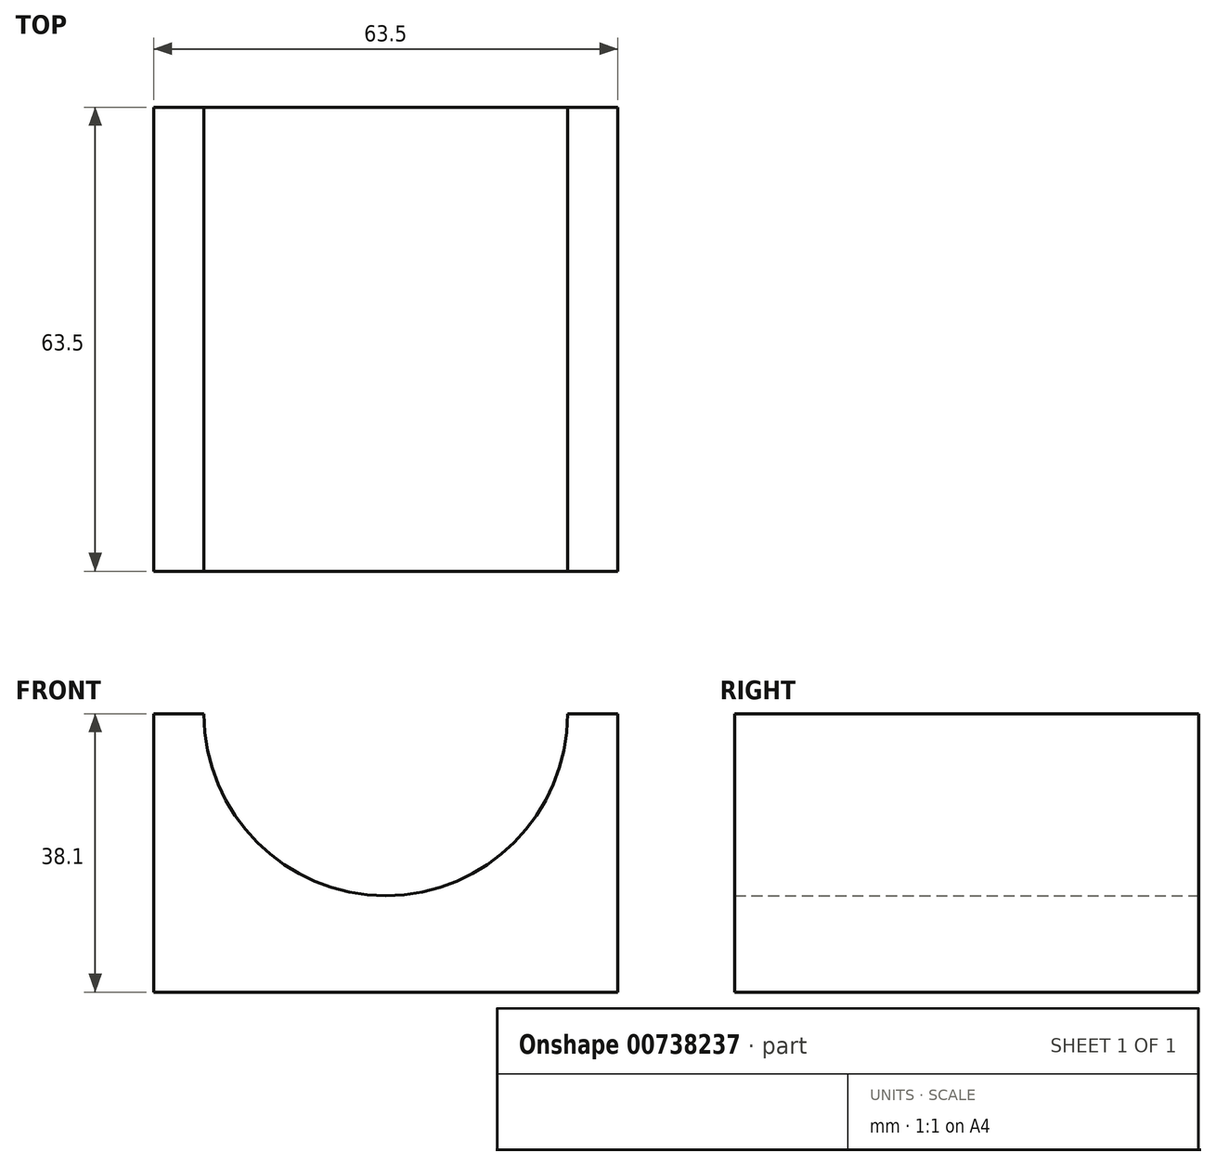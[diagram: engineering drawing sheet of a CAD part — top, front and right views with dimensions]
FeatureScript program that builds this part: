
annotation { "Feature Type Name" : "Feature", "Feature Type Description" : "" }
export const myFeature = defineFeature(function(context is Context, id is Id, definition is map)
    precondition{}
    {
        {
            var Q0;
            Q0=qCreatedBy(makeId("Front.planeOp"),FACE);
            var sketch = newSketch(context, id + "F0", { "sketchPlane" : qUnion([Q0])});
            skLineSegment(sketch, "E0.bottom", {"start": v(-33.25, 15.52) * mm, "end": v(30.25, 15.52) * mm});
            skLineSegment(sketch, "E0.top", {"start": v(-33.25, -22.58) * mm, "end": v(30.25, -22.58) * mm});
            skLineSegment(sketch, "E0.left", {"start": v(-33.25, 15.52) * mm, "end": v(-33.25, -22.58) * mm});
            skLineSegment(sketch, "E0.right", {"start": v(30.25, 15.52) * mm, "end": v(30.25, -22.58) * mm});
            skArc(sketch, "E1", {"start": v(-26.4, 15.52) * mm, "mid": v(-1.5, -9.37) * mm, "end": v(23.4, 15.52) * mm});
            skSolve(sketch);
        }
        {
            var Q0;
            Q0=makeQuery(id+"F0.imprint","IMPRINT",FACE,{"disambiguationData":[TD([[makeQuery(id+"F0.imprint","IMPRINT",EDGE,{"derivedFrom":sQuery(id+"F0.wireOp",EDGE,"E0.top")}),1.0]])]});
            extrude(context, id + "F1", {"entities" : qUnion([Q0]), "depth" : 63.5 * mm, "offsetDistance" : 25.4 * mm});
        }
    });
